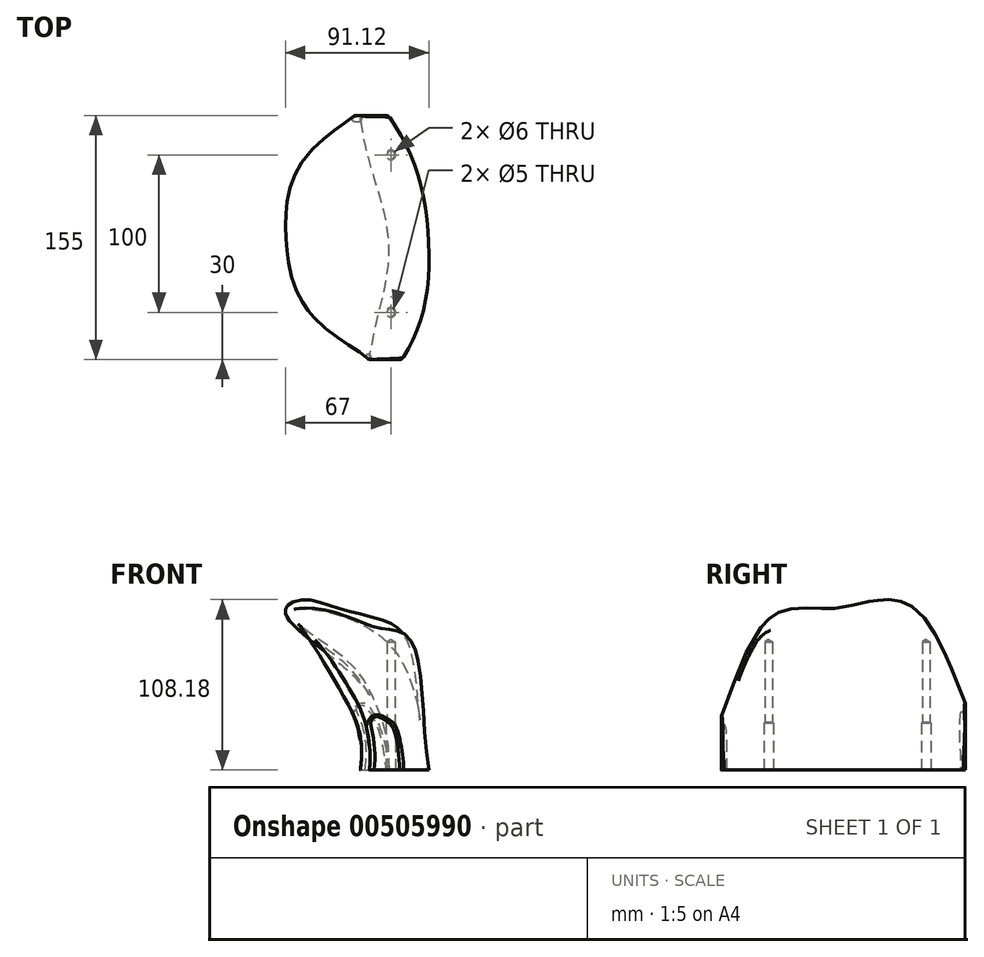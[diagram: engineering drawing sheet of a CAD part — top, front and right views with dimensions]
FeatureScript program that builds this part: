
annotation { "Feature Type Name" : "Feature", "Feature Type Description" : "" }
export const myFeature = defineFeature(function(context is Context, id is Id, definition is map)
    precondition{}
    {
        {
            var Q0;
            Q0=qCreatedBy(makeId("Top.planeOp"),FACE);
            var sketch = newSketch(context, id + "F0", { "sketchPlane" : qUnion([Q0])});
            skLineSegment(sketch, "E0", {"start": v(-5.76, 80.72) * mm, "end": v(0.76, -70) * mm, "construction": true});
            skPoint(sketch, "E1", {"position": v(0, 60) * mm});
            skPoint(sketch, "E2", {"position": v(27.6, 60) * mm});
            skPoint(sketch, "E3", {"position": v(4.93, -45) * mm});
            skPoint(sketch, "E4", {"position": v(32.14, -45) * mm});
            skPoint(sketch, "E5", {"position": v(13.5, 0) * mm});
            skPoint(sketch, "E6", {"position": v(39.06, 0) * mm});
            skFitSpline(sketch, "E7", {"points": [v(-5.76, 80.72) * mm, v(13.45, 15.87) * mm, v(0.76, -70) * mm, v(7.29, -83.4) * mm, v(22.14, -70) * mm, v(38.45, 17.68) * mm, v(13.45, 85) * mm, v(1.85, 91.96) * mm, v(-5.76, 80.72) * mm]});
            skSolve(sketch);
        }
        {
            var Q0;
            Q0=qCreatedBy(makeId("Front.planeOp"),FACE);
            var sketch = newSketch(context, id + "F1", { "sketchPlane" : qUnion([Q0])});
            skLineSegment(sketch, "E8", {"start": v(39.06, 0) * mm, "end": v(13.5, 0) * mm});
            skFitSpline(sketch, "E9", {"points": [v(39.06, 0) * mm, v(30.6, 47.23) * mm, v(0, 90.7) * mm, v(-50.94, 100) * mm, v(-19.22, 68.97) * mm, v(6.47, 38.97) * mm, v(13.5, 0) * mm], "startDerivative": vector(-66.25, 337.68) * mm, "endDerivative": vector(-26.67, -266.15) * mm});
            skSolve(sketch);
        }
        {
            var Q0;
            Q0=qCreatedBy(makeId("Front.planeOp"),FACE);
            cPlane(context, id + "F2", {"entities" : qUnion([Q0]), "cplaneType" : CPlaneType.OFFSET, "offset" : 45 * mm, "width" : 150 * mm, "height" : 150 * mm});
        }
        {
            var Q0;
            Q0=qCreatedBy(makeId("Front.planeOp"),FACE);
            cPlane(context, id + "F3", {"entities" : qUnion([Q0]), "cplaneType" : CPlaneType.OFFSET, "offset" : 60 * mm, "oppositeDirection" : true, "width" : 150 * mm, "height" : 150 * mm});
        }
        {
            var Q0;
            Q0=qCreatedBy(id+"F3.planeOp",FACE);
            var sketch = newSketch(context, id + "F4", { "sketchPlane" : qUnion([Q0])});
            skLineSegment(sketch, "E10", {"start": v(27.6, 0) * mm, "end": v(0, 0) * mm});
            skFitSpline(sketch, "E11", {"points": [v(0, 0) * mm, v(-2.22, 44.92) * mm, v(-20.07, 69.43) * mm, v(-38.14, 86.6) * mm, v(-29.27, 95.03) * mm, v(-14.41, 90.6) * mm, v(18.95, 83.16) * mm, v(27.6, 0) * mm], "startDerivative": vector(-9.91, 282.97) * mm, "endDerivative": vector(58.43, -395.82) * mm});
            skSolve(sketch);
        }
        {
            var Q0;
            Q0=qCreatedBy(id+"F2.planeOp",FACE);
            var sketch = newSketch(context, id + "F5", { "sketchPlane" : qUnion([Q0])});
            skFitSpline(sketch, "E12", {"points": [v(33.9, 0) * mm, v(25.6, 81.4) * mm, v(2.46, 83.85) * mm, v(-20.1, 90.03) * mm, v(-31.72, 88.25) * mm, v(-28.15, 76.63) * mm, v(-10.28, 60.55) * mm, v(4.02, 31.73) * mm, v(5.88, 0) * mm], "startDerivative": vector(-18.45, 356.23) * mm, "endDerivative": vector(-36.58, -284.24) * mm});
            skLineSegment(sketch, "E13", {"start": v(5.88, 0) * mm, "end": v(33.9, 0) * mm});
            skSolve(sketch);
        }
        {
            var Q0;
            Q0=qCreatedBy(id+"F2.planeOp",FACE);
            cPlane(context, id + "F6", {"entities" : qUnion([Q0]), "cplaneType" : CPlaneType.OFFSET, "offset" : 25 * mm, "width" : 150 * mm, "height" : 150 * mm});
        }
        {
            var Q0;
            Q0=qCreatedBy(id+"F3.planeOp",FACE);
            cPlane(context, id + "F7", {"entities" : qUnion([Q0]), "cplaneType" : CPlaneType.OFFSET, "offset" : 25 * mm, "oppositeDirection" : true, "width" : 150 * mm, "height" : 150 * mm});
        }
        {
            var Q0;
            Q0=qCreatedBy(id+"F6.planeOp",FACE);
            var sketch = newSketch(context, id + "F8", { "sketchPlane" : qUnion([Q0])});
            skLineSegment(sketch, "E14", {"start": v(0.76, 0) * mm, "end": v(22.14, 0) * mm});
            skFitSpline(sketch, "E15", {"points": [v(22.14, 0) * mm, v(20.05, 18) * mm, v(16.18, 28.93) * mm, v(5.45, 34.48) * mm, v(1.28, 30.5) * mm, v(1.06, 14.72) * mm, v(0.76, 0) * mm], "startDerivative": vector(1.3, 84.38) * mm, "endDerivative": vector(-6.04, -79.6) * mm});
            skSolve(sketch);
        }
        {
            var Q0;
            Q0=qCreatedBy(id+"F7.planeOp",FACE);
            var sketch = newSketch(context, id + "F9", { "sketchPlane" : qUnion([Q0])});
            skLineSegment(sketch, "E16", {"start": v(-5, 0) * mm, "end": v(13.45, 0) * mm});
            skFitSpline(sketch, "E17", {"points": [v(13.45, 0) * mm, v(8.38, 24.1) * mm, v(-2.03, 41.65) * mm, v(-7.46, 39.52) * mm, v(-6.02, 27.12) * mm, v(-4.06, 6.58) * mm, v(-5, 0) * mm], "startDerivative": vector(-17.77, 109.52) * mm, "endDerivative": vector(-14.07, -52.15) * mm});
            skSolve(sketch);
        }
        {
            var Q0;
            Q0=makeQuery(id+"F9.imprint","IMPRINT",FACE,{"disambiguationData":[TD([[makeQuery(id+"F9.imprint","IMPRINT",EDGE,{"derivedFrom":sQuery(id+"F9.wireOp",EDGE,"E16")}),1.0]])]});
            var Q1;
            Q1=makeQuery(id+"F4.imprint","IMPRINT",FACE,{"disambiguationData":[TD([[makeQuery(id+"F4.imprint","IMPRINT",EDGE,{"derivedFrom":sQuery(id+"F4.wireOp",EDGE,"E10")}),-1.0]])]});
            var Q2;
            Q2=makeQuery(id+"F1.imprint","IMPRINT",FACE,{"disambiguationData":[TD([[makeQuery(id+"F1.imprint","IMPRINT",EDGE,{"derivedFrom":sQuery(id+"F1.wireOp",EDGE,"E8")}),-1.0]])]});
            var Q3;
            Q3=makeQuery(id+"F5.imprint","IMPRINT",FACE,{"disambiguationData":[TD([[makeQuery(id+"F5.imprint","IMPRINT",EDGE,{"derivedFrom":sQuery(id+"F5.wireOp",EDGE,"E12")}),1.0]])]});
            var Q4;
            Q4=makeQuery(id+"F8.imprint","IMPRINT",FACE,{"disambiguationData":[TD([[makeQuery(id+"F8.imprint","IMPRINT",EDGE,{"derivedFrom":sQuery(id+"F8.wireOp",EDGE,"E15")}),1.0]])]});
            loft(context, id + "F10", {"sheetProfilesArray" : [{ "sheetProfileEntities" : qUnion([Q0]) }, { "sheetProfileEntities" : qUnion([Q1]) }, { "sheetProfileEntities" : qUnion([Q2]) }, { "sheetProfileEntities" : qUnion([Q3]) }, { "sheetProfileEntities" : qUnion([Q4]) }]});
        }
        {
            var Q0;
            {var subQ0=sQuery(id+"F8.wireOp",EDGE,"E15");var subQ1=sQuery(id+"F8.wireOp",EDGE,"E14");Q0=makeQuery(id+"F10.opLoft","MID_CAP_EDGE",EDGE,{"disambiguationData":[OSD([subQ0,subQ1]),TDD([makeQuery(id+"F8.imprint","INTERSECT",VERTEX,{"disambiguationData":[OD(0.0)],"derivedFrom":[subQ0,subQ1]}),makeQuery(id+"F8.imprint","INTERSECT",VERTEX,{"disambiguationData":[OD(1.0)],"derivedFrom":[subQ0,subQ1]}),makeQuery(id+"F8.imprint","IMPRINT",EDGE,{"derivedFrom":subQ0})])],"capPos":4.0});}
            fillet(context, id + "F11", {"entities" : qUnion([Q0]), "radius" : 3 * mm, "tangentPropagation" : true, "allowEdgeOverflow" : false});
        }
        {
            var Q0;
            {var subQ0=sQuery(id+"F9.wireOp",EDGE,"E17");var subQ1=sQuery(id+"F9.wireOp",EDGE,"E16");Q0=makeQuery(id+"F10.opLoft","MID_CAP_EDGE",EDGE,{"disambiguationData":[OSD([subQ1,subQ0]),TDD([makeQuery(id+"F9.imprint","INTERSECT",VERTEX,{"disambiguationData":[OD(0.0)],"derivedFrom":[subQ1,subQ0]}),makeQuery(id+"F9.imprint","INTERSECT",VERTEX,{"disambiguationData":[OD(1.0)],"derivedFrom":[subQ1,subQ0]}),makeQuery(id+"F9.imprint","IMPRINT",EDGE,{"derivedFrom":subQ0})])],"capPos":0.0});}
            fillet(context, id + "F12", {"entities" : qUnion([Q0]), "radius" : 3 * mm, "tangentPropagation" : true, "allowEdgeOverflow" : false});
        }
        {
            var Q0;
            Q0=makeQuery(id+"F0.imprint","IMPRINT",FACE,{"disambiguationData":[TD([[makeQuery(id+"F0.imprint","IMPRINT",EDGE,{"derivedFrom":sQuery(id+"F0.wireOp",EDGE,"E7")}),1.0]])]});
            var sketch = newSketch(context, id + "F13", { "sketchPlane" : qUnion([Q0])});
            skPoint(sketch, "E18", {"position": v(15, -40) * mm});
            skPoint(sketch, "E19", {"position": v(15, 60) * mm});
            skSolve(sketch);
        }
        {
            var Q0;
            Q0=sQuery(id+"F13.wireOp",VERTEX,"E18");
            var Q1;
            Q1=sQuery(id+"F13.wireOp",VERTEX,"E19");
            var Q2;
            Q2=makeQuery(id+"F10.opLoft","SWEPT_BODY",BODY,{"disambiguationData":[OSD([sQuery(id+"F1.wireOp",EDGE,"E8"),sQuery(id+"F4.wireOp",EDGE,"E11"),sQuery(id+"F5.wireOp",EDGE,"E12"),makeQuery(id+"F8.imprint","IMPRINT",FACE,{"disambiguationData":[TD([[makeQuery(id+"F8.imprint","IMPRINT",EDGE,{"derivedFrom":sQuery(id+"F8.wireOp",EDGE,"E15")}),1.0]])]}),makeQuery(id+"F9.imprint","IMPRINT",FACE,{"disambiguationData":[TD([[makeQuery(id+"F9.imprint","IMPRINT",EDGE,{"derivedFrom":sQuery(id+"F9.wireOp",EDGE,"E16")}),1.0]])]})])]});
            hole(context, id + "F14", {"style" : HoleStyle.SIMPLE, "endStyle" : HoleEndStyle.BLIND, "oppositeDirection" : true, "holeDiameter" : 6 * mm, "holeDepth" : 30 * mm, "isTappedThrough" : true, "tappedDepth" : 12 * mm, "tapClearance" : 3, "locations" : qUnion([Q0, Q1]), "scope" : qUnion([Q2]), "majorDiameter" : 5 * mm});
        }
        {
            var Q0;
            Q0=sQuery(id+"F13.wireOp",VERTEX,"E19");
            var Q1;
            Q1=sQuery(id+"F13.wireOp",VERTEX,"E18");
            var Q2;
            Q2=makeQuery(id+"F10.opLoft","SWEPT_BODY",BODY,{"disambiguationData":[OSD([sQuery(id+"F1.wireOp",EDGE,"E8"),sQuery(id+"F4.wireOp",EDGE,"E11"),sQuery(id+"F5.wireOp",EDGE,"E12"),makeQuery(id+"F8.imprint","IMPRINT",FACE,{"disambiguationData":[TD([[makeQuery(id+"F8.imprint","IMPRINT",EDGE,{"derivedFrom":sQuery(id+"F8.wireOp",EDGE,"E15")}),1.0]])]}),makeQuery(id+"F9.imprint","IMPRINT",FACE,{"disambiguationData":[TD([[makeQuery(id+"F9.imprint","IMPRINT",EDGE,{"derivedFrom":sQuery(id+"F9.wireOp",EDGE,"E16")}),1.0]])]})])]});
            hole(context, id + "F15", {"style" : HoleStyle.SIMPLE, "endStyle" : HoleEndStyle.BLIND, "oppositeDirection" : true, "holeDiameter" : 5 * mm, "holeDepth" : 51 * mm, "isTappedThrough" : true, "tappedDepth" : 12 * mm, "tapClearance" : 3, "locations" : qUnion([Q0, Q1]), "scope" : qUnion([Q2]), "majorDiameter" : 5 * mm});
        }
    });
